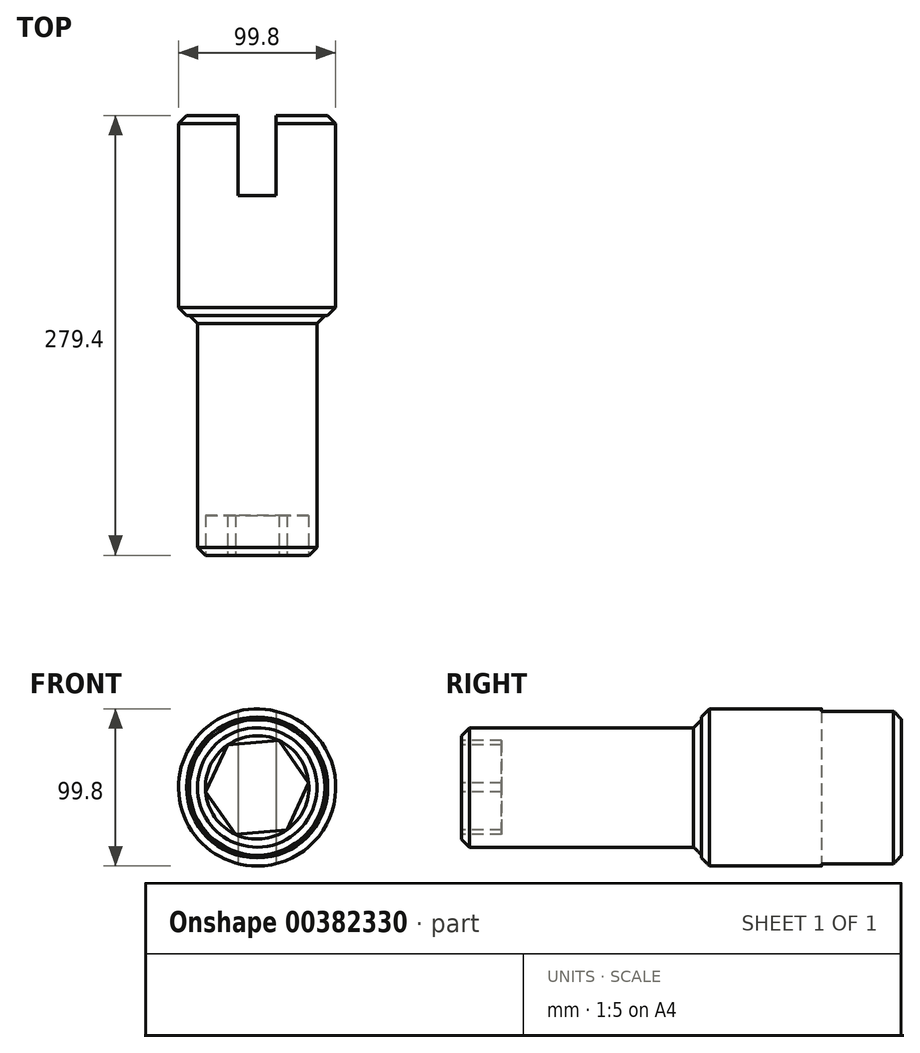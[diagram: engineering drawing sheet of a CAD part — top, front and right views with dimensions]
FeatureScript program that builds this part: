
annotation { "Feature Type Name" : "Feature", "Feature Type Description" : "" }
export const myFeature = defineFeature(function(context is Context, id is Id, definition is map)
    precondition{}
    {
        {
            var Q0;
            Q0=qCreatedBy(makeId("Front.planeOp"),FACE);
            var sketch = newSketch(context, id + "F0", { "sketchPlane" : qUnion([Q0])});
            skCircle(sketch, "E0", {"center": v(0, 0) * mm, "radius": 49.9 * mm});
            skSolve(sketch);
        }
        {
            var Q0;
            Q0 = qSketchRegion(id + "F0", true);
            extrude(context, id + "F1", {"entities" : qUnion([Q0]), "depth" : 127 * mm});
        }
        {
            var Q0;
            Q0=makeQuery(id+"F1.opExtrude","CAP_FACE",FACE,{"disambiguationData":[OSD([sQuery(id+"F0.wireOp",EDGE,"E0")])],"isStart":false});
            var sketch = newSketch(context, id + "F2", { "sketchPlane" : qUnion([Q0])});
            skCircle(sketch, "E1", {"center": v(0, 0) * mm, "radius": 37.92 * mm});
            skSolve(sketch);
        }
        {
            var Q0;
            Q0 = qSketchRegion(id + "F2", true);
            extrude(context, id + "F3", {"entities" : qUnion([Q0]), "operationType" : NewBodyOperationType.ADD, "depth" : 152.4 * mm});
        }
        {
            var Q0;
            Q0=makeQuery(id+"F1.opExtrude","CAP_FACE",FACE,{"disambiguationData":[OSD([sQuery(id+"F0.wireOp",EDGE,"E0")])],"isStart":false});
            var Q1;
            Q1=makeQuery(id+"F3.opExtrude","CAP_EDGE",EDGE,{"disambiguationData":[OSD([sQuery(id+"F2.wireOp",EDGE,"E1")])],"isStart":false});
            var Q2;
            Q2=makeQuery(id+"F1.opExtrude","CAP_EDGE",EDGE,{"disambiguationData":[OSD([sQuery(id+"F0.wireOp",EDGE,"E0")])],"isStart":true});
            chamfer(context, id + "F4", {"entities" : qUnion([Q0, Q1, Q2]), "width" : 5.08 * mm, "tangentPropagation" : true});
        }
        {
            var Q0;
            Q0=makeQuery(id+"F3.opExtrude","CAP_FACE",FACE,{"disambiguationData":[OSD([sQuery(id+"F2.wireOp",EDGE,"E1")])],"isStart":false});
            var sketch = newSketch(context, id + "F5", { "sketchPlane" : qUnion([Q0])});
            skCircle(sketch, "E2.cCircle", {"center": v(0, 0) * mm, "radius": 32.84 * mm, "construction": true});
            skLineSegment(sketch, "E2.0", {"start": v(18.84, -26.9) * mm, "end": v(-13.88, -29.77) * mm});
            skLineSegment(sketch, "E2.1", {"start": v(-13.88, -29.77) * mm, "end": v(-32.72, -2.86) * mm});
            skLineSegment(sketch, "E2.2", {"start": v(-32.72, -2.86) * mm, "end": v(-18.84, 26.9) * mm});
            skLineSegment(sketch, "E2.3", {"start": v(-18.84, 26.9) * mm, "end": v(13.88, 29.77) * mm});
            skLineSegment(sketch, "E2.4", {"start": v(13.88, 29.77) * mm, "end": v(32.72, 2.86) * mm});
            skLineSegment(sketch, "E2.5", {"start": v(32.72, 2.86) * mm, "end": v(18.84, -26.9) * mm});
            skSolve(sketch);
        }
        {
            var Q0;
            Q0 = qSketchRegion(id + "F5", true);
            extrude(context, id + "F6", {"entities" : qUnion([Q0]), "operationType" : NewBodyOperationType.REMOVE, "oppositeDirection" : true, "depth" : 25.4 * mm});
        }
        {
            var Q0;
            Q0=makeQuery(id+"F1.opExtrude","CAP_FACE",FACE,{"disambiguationData":[OSD([sQuery(id+"F0.wireOp",EDGE,"E0")])],"isStart":true});
            var sketch = newSketch(context, id + "F7", { "sketchPlane" : qUnion([Q0])});
            skLineSegment(sketch, "E3.bottom", {"start": v(8.36, -44.03) * mm, "end": v(-8.36, -44.03) * mm});
            skLineSegment(sketch, "E3.top", {"start": v(8.36, 44.03) * mm, "end": v(-8.36, 44.03) * mm});
            skLineSegment(sketch, "E3.left", {"start": v(8.36, -44.03) * mm, "end": v(8.36, 44.03) * mm});
            skLineSegment(sketch, "E3.right", {"start": v(-8.36, -44.03) * mm, "end": v(-8.36, 44.03) * mm});
            skPoint(sketch, "E3.middle", {"position": v(0, 0) * mm});
            skSolve(sketch);
        }
        {
            var Q0;
            Q0=sQuery(id+"F7.wireOp",EDGE,"E3.top");
            extrude(context, id + "F8", {"bodyType" : ToolBodyType.SURFACE, "surfaceEntities" : qUnion([Q0]), "oppositeDirection" : true, "depth" : 25.4 * mm});
        }
        {
            var Q0;
            Q0=makeQuery(id+"F1.opExtrude","CAP_FACE",FACE,{"disambiguationData":[OSD([sQuery(id+"F0.wireOp",EDGE,"E0")])],"isStart":true});
            var sketch = newSketch(context, id + "F9", { "sketchPlane" : qUnion([Q0])});
            skLineSegment(sketch, "E4.bottom", {"start": v(-12.07, 64.89) * mm, "end": v(12.07, 64.89) * mm});
            skLineSegment(sketch, "E4.top", {"start": v(-12.07, -64.89) * mm, "end": v(12.07, -64.89) * mm});
            skLineSegment(sketch, "E4.left", {"start": v(-12.07, 64.89) * mm, "end": v(-12.07, -64.89) * mm});
            skLineSegment(sketch, "E4.right", {"start": v(12.07, 64.89) * mm, "end": v(12.07, -64.89) * mm});
            skPoint(sketch, "E4.middle", {"position": v(0, 0) * mm});
            skSolve(sketch);
        }
        {
            var Q0;
            Q0 = qSketchRegion(id + "F9", true);
            extrude(context, id + "F10", {"entities" : qUnion([Q0]), "operationType" : NewBodyOperationType.REMOVE, "oppositeDirection" : true, "depth" : 50.8 * mm});
        }
        {
            var Q0;
            Q0=makeQuery(id+"F8.opExtrude","SWEPT_BODY",BODY,{"disambiguationData":[OSD([sQuery(id+"F7.wireOp",EDGE,"E3.top")])]});
            deleteBodies(context, id + "F11", {"entities" : qUnion([Q0])});
        }
    });
